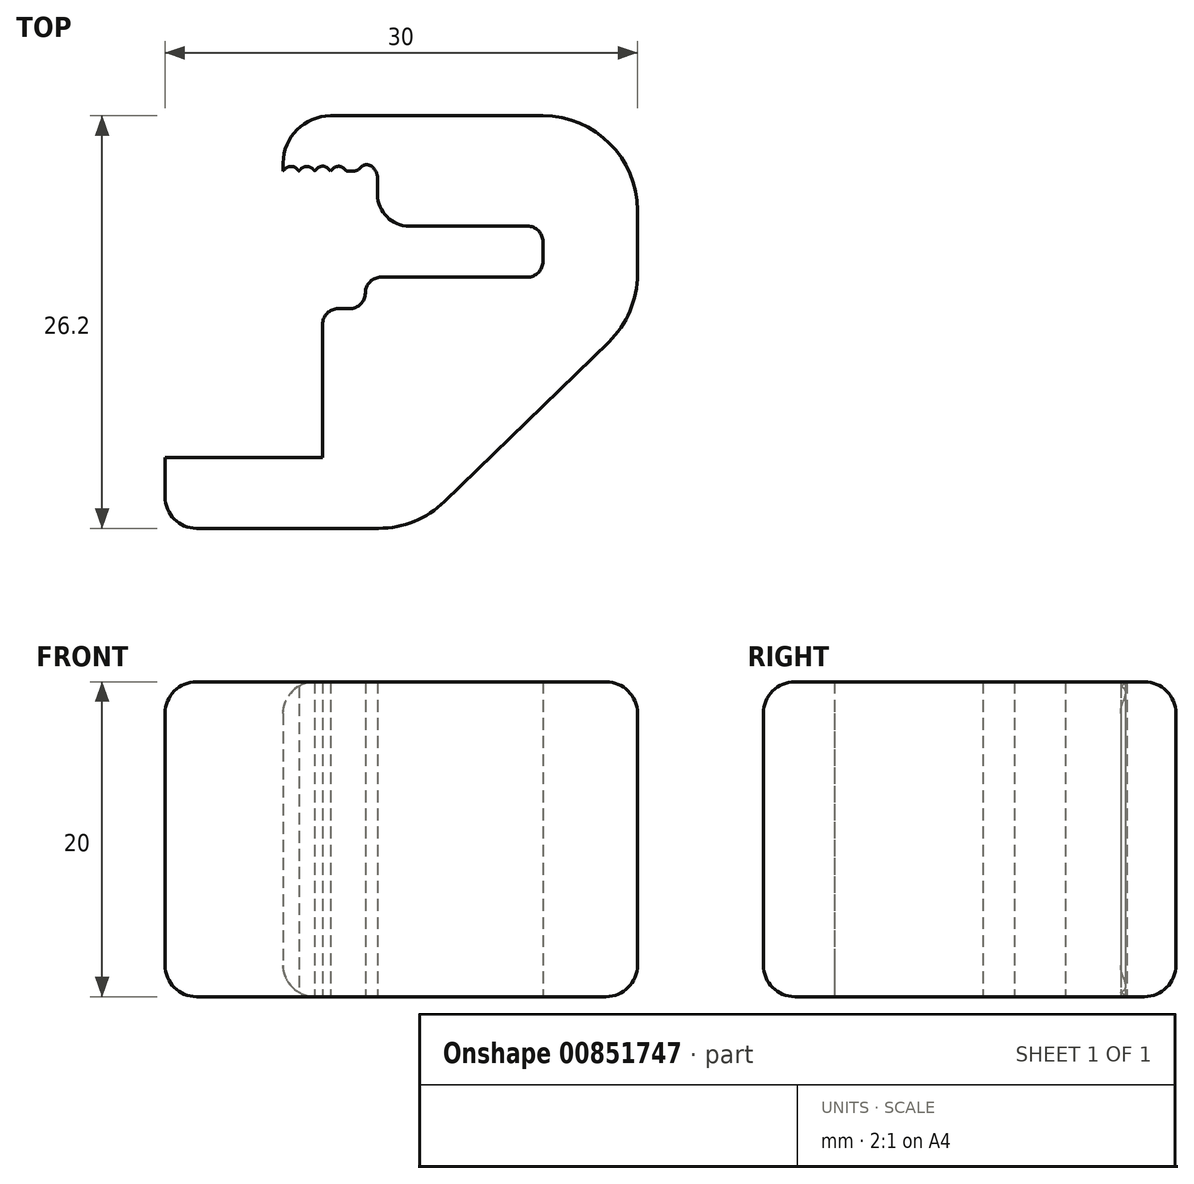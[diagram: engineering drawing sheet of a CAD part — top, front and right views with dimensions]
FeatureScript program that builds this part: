
annotation { "Feature Type Name" : "Feature", "Feature Type Description" : "" }
export const myFeature = defineFeature(function(context is Context, id is Id, definition is map)
    precondition{}
    {
        {
            var Q0;
            Q0=qCreatedBy(makeId("Top.planeOp"),FACE);
            var sketch = newSketch(context, id + "F0", { "sketchPlane" : qUnion([Q0])});
            skLineSegment(sketch, "E0", {"start": v(-33, 18.72) * mm, "end": v(-33, 17.72) * mm});
            skLineSegment(sketch, "E1", {"start": v(-31, 15.72) * mm, "end": v(-23.5, 15.72) * mm});
            skLineSegment(sketch, "E2", {"start": v(-22.5, 14.72) * mm, "end": v(-22.5, 13.47) * mm});
            skLineSegment(sketch, "E3", {"start": v(-36.5, 9.47) * mm, "end": v(-36.5, 2.97) * mm});
            skLineSegment(sketch, "E4", {"start": v(-46.5, 0.52) * mm, "end": v(-46.5, -1.48) * mm});
            skLineSegment(sketch, "E5", {"start": v(-44.5, -3.48) * mm, "end": v(-32.94, -3.48) * mm});
            skLineSegment(sketch, "E6", {"start": v(-39, 19.72) * mm, "end": v(-39, 19.72) * mm});
            skLineSegment(sketch, "E7", {"start": v(-36, 22.72) * mm, "end": v(-22.5, 22.72) * mm});
            skPoint(sketch, "E8.visualSharp", {"position": v(-39, 22.72) * mm});
            skArc(sketch, "E8.filletArc", {"start": v(-36, 22.72) * mm, "mid": v(-38.12, 21.84) * mm, "end": v(-39, 19.72) * mm});
            skPoint(sketch, "E9.visualSharp", {"position": v(-46.5, -3.48) * mm});
            skArc(sketch, "E9.filletArc", {"start": v(-46.5, -1.48) * mm, "mid": v(-45.92, -2.9) * mm, "end": v(-44.5, -3.48) * mm});
            skPoint(sketch, "E10.visualSharp", {"position": v(-36.5, 12.47) * mm});
            skPoint(sketch, "E11.visualSharp", {"position": v(-33, 15.72) * mm});
            skArc(sketch, "E11.filletArc", {"start": v(-33, 17.72) * mm, "mid": v(-32.42, 16.3) * mm, "end": v(-31, 15.72) * mm});
            skPoint(sketch, "E12.visualSharp", {"position": v(-33, 19.72) * mm});
            skArc(sketch, "E12.filletArc", {"start": v(-33, 18.72) * mm, "mid": v(-33.1, 19.16) * mm, "end": v(-33.4, 19.52) * mm});
            skPoint(sketch, "E13.visualSharp", {"position": v(-22.5, 15.72) * mm});
            skArc(sketch, "E13.filletArc", {"start": v(-22.5, 14.72) * mm, "mid": v(-22.8, 15.42) * mm, "end": v(-23.5, 15.72) * mm});
            skPoint(sketch, "E14.visualSharp", {"position": v(-22.5, 12.47) * mm});
            skArc(sketch, "E14.filletArc", {"start": v(-23.5, 12.47) * mm, "mid": v(-22.8, 12.76) * mm, "end": v(-22.5, 13.47) * mm});
            skLineSegment(sketch, "E15", {"start": v(-33.78, 11.47) * mm, "end": v(-33.78, 11.47) * mm});
            skLineSegment(sketch, "E16", {"start": v(-34.78, 10.47) * mm, "end": v(-35.5, 10.47) * mm});
            skLineSegment(sketch, "E17", {"start": v(-32.78, 12.47) * mm, "end": v(-23.5, 12.47) * mm});
            skPoint(sketch, "E18.visualSharp", {"position": v(-33.78, 12.47) * mm});
            skArc(sketch, "E18.filletArc", {"start": v(-32.78, 12.47) * mm, "mid": v(-33.49, 12.17) * mm, "end": v(-33.78, 11.47) * mm});
            skPoint(sketch, "E19.visualSharp", {"position": v(-36.5, 10.47) * mm});
            skArc(sketch, "E19.filletArc", {"start": v(-35.5, 10.47) * mm, "mid": v(-36.2, 10.17) * mm, "end": v(-36.5, 9.47) * mm});
            skPoint(sketch, "E20.visualSharp", {"position": v(-33.78, 10.47) * mm});
            skArc(sketch, "E20.filletArc", {"start": v(-34.78, 10.47) * mm, "mid": v(-34.07, 10.76) * mm, "end": v(-33.78, 11.47) * mm});
            skLineSegment(sketch, "E21", {"start": v(-16.5, 16.72) * mm, "end": v(-16.5, 12.65) * mm});
            skLineSegment(sketch, "E22", {"start": v(-18.32, 8.35) * mm, "end": v(-28.76, -1.79) * mm});
            skPoint(sketch, "E23.visualSharp", {"position": v(-16.5, 22.72) * mm});
            skArc(sketch, "E23.filletArc", {"start": v(-16.5, 16.72) * mm, "mid": v(-18.26, 20.96) * mm, "end": v(-22.5, 22.72) * mm});
            skPoint(sketch, "E24.visualSharp", {"position": v(-16.5, 10.12) * mm});
            skArc(sketch, "E24.filletArc", {"start": v(-18.32, 8.35) * mm, "mid": v(-16.97, 10.32) * mm, "end": v(-16.5, 12.65) * mm});
            skPoint(sketch, "E25.visualSharp", {"position": v(-30.5, -3.48) * mm});
            skArc(sketch, "E25.filletArc", {"start": v(-32.94, -3.48) * mm, "mid": v(-30.68, -3.04) * mm, "end": v(-28.76, -1.79) * mm});
            skLineSegment(sketch, "E26", {"start": v(-39, 19.72) * mm, "end": v(-39, 19.22) * mm});
            skLineSegment(sketch, "E27", {"start": v(-34.94, 19.22) * mm, "end": v(-34.5, 19.22) * mm});
            skLineSegment(sketch, "E28", {"start": v(-39, 19.22) * mm, "end": v(-38.85, 19.36) * mm});
            skLineSegment(sketch, "E29", {"start": v(-38.15, 19.36) * mm, "end": v(-38, 19.22) * mm});
            skLineSegment(sketch, "E30", {"start": v(-38, 19.22) * mm, "end": v(-37.85, 19.36) * mm});
            skLineSegment(sketch, "E31", {"start": v(-37.15, 19.36) * mm, "end": v(-37, 19.22) * mm});
            skLineSegment(sketch, "E32", {"start": v(-37, 19.22) * mm, "end": v(-36.85, 19.37) * mm});
            skLineSegment(sketch, "E33", {"start": v(-36.15, 19.38) * mm, "end": v(-35.98, 19.22) * mm});
            skLineSegment(sketch, "E34", {"start": v(-35.98, 19.22) * mm, "end": v(-35.84, 19.36) * mm});
            skLineSegment(sketch, "E35", {"start": v(-35.14, 19.37) * mm, "end": v(-35, 19.25) * mm});
            skArc(sketch, "E36.filletArc", {"start": v(-38.15, 19.36) * mm, "mid": v(-38.5, 19.51) * mm, "end": v(-38.85, 19.36) * mm});
            skArc(sketch, "E37.filletArc", {"start": v(-37.15, 19.36) * mm, "mid": v(-37.5, 19.51) * mm, "end": v(-37.85, 19.36) * mm});
            skArc(sketch, "E38.filletArc", {"start": v(-36.15, 19.38) * mm, "mid": v(-36.5, 19.52) * mm, "end": v(-36.85, 19.37) * mm});
            skArc(sketch, "E39.filletArc", {"start": v(-35.14, 19.37) * mm, "mid": v(-35.5, 19.51) * mm, "end": v(-35.84, 19.36) * mm});
            skArc(sketch, "E40.filletArc", {"start": v(-35, 19.25) * mm, "mid": v(-34.97, 19.22) * mm, "end": v(-34.94, 19.22) * mm});
            skPoint(sketch, "E41.visualSharp", {"position": v(-34, 19.22) * mm});
            skArc(sketch, "E41.filletArc", {"start": v(-34.5, 19.22) * mm, "mid": v(-34.28, 19.27) * mm, "end": v(-34.1, 19.42) * mm});
            skArc(sketch, "E42.filletArc", {"start": v(-33.4, 19.52) * mm, "mid": v(-33.77, 19.61) * mm, "end": v(-34.1, 19.42) * mm});
            skLineSegment(sketch, "E43", {"start": v(-46.5, 0.52) * mm, "end": v(-46.5, 1.02) * mm});
            skLineSegment(sketch, "E44", {"start": v(-46.5, 1.02) * mm, "end": v(-38.5, 1.02) * mm});
            skLineSegment(sketch, "E45", {"start": v(-36.5, 2.97) * mm, "end": v(-36.5, 1.02) * mm});
            skLineSegment(sketch, "E46", {"start": v(-36.5, 1.02) * mm, "end": v(-38.5, 1.02) * mm});
            skSolve(sketch);
        }
        {
            var Q0;
            Q0=makeQuery(id+"F0.imprint","IMPRINT",FACE,{"disambiguationData":[TD([[makeQuery(id+"F0.imprint","IMPRINT",EDGE,{"derivedFrom":sQuery(id+"F0.wireOp",EDGE,"Ief0eZWC-VvyC-w0M1-CLn9-HvXQDqPH4N7M")}),1.0]])]});
            var Q1;
            Q1=makeQuery(id+"F0.imprint","IMPRINT",FACE,{"disambiguationData":[TD([[makeQuery(id+"F0.imprint","IMPRINT",EDGE,{"derivedFrom":sQuery(id+"F0.wireOp",EDGE,"E0")}),1.0]])]});
            extrude(context, id + "F1", {"entities" : qUnion([Q0, Q1]), "depth" : 20 * mm, "offsetDistance" : 25 * mm});
        }
        {
            var Q0;
            Q0=makeQuery(id+"F1.opExtrude","CAP_EDGE",EDGE,{"disambiguationData":[OSD([sQuery(id+"F0.wireOp",EDGE,"E7")])],"isStart":false});
            var Q1;
            Q1=makeQuery(id+"F1.opExtrude","CAP_EDGE",EDGE,{"disambiguationData":[OSD([sQuery(id+"F0.wireOp",EDGE,"E7")])],"isStart":true});
            fillet(context, id + "F2", {"entities" : qUnion([Q0, Q1]), "radius" : 2 * mm, "tangentPropagation" : true, "allowEdgeOverflow" : false});
        }
    });
